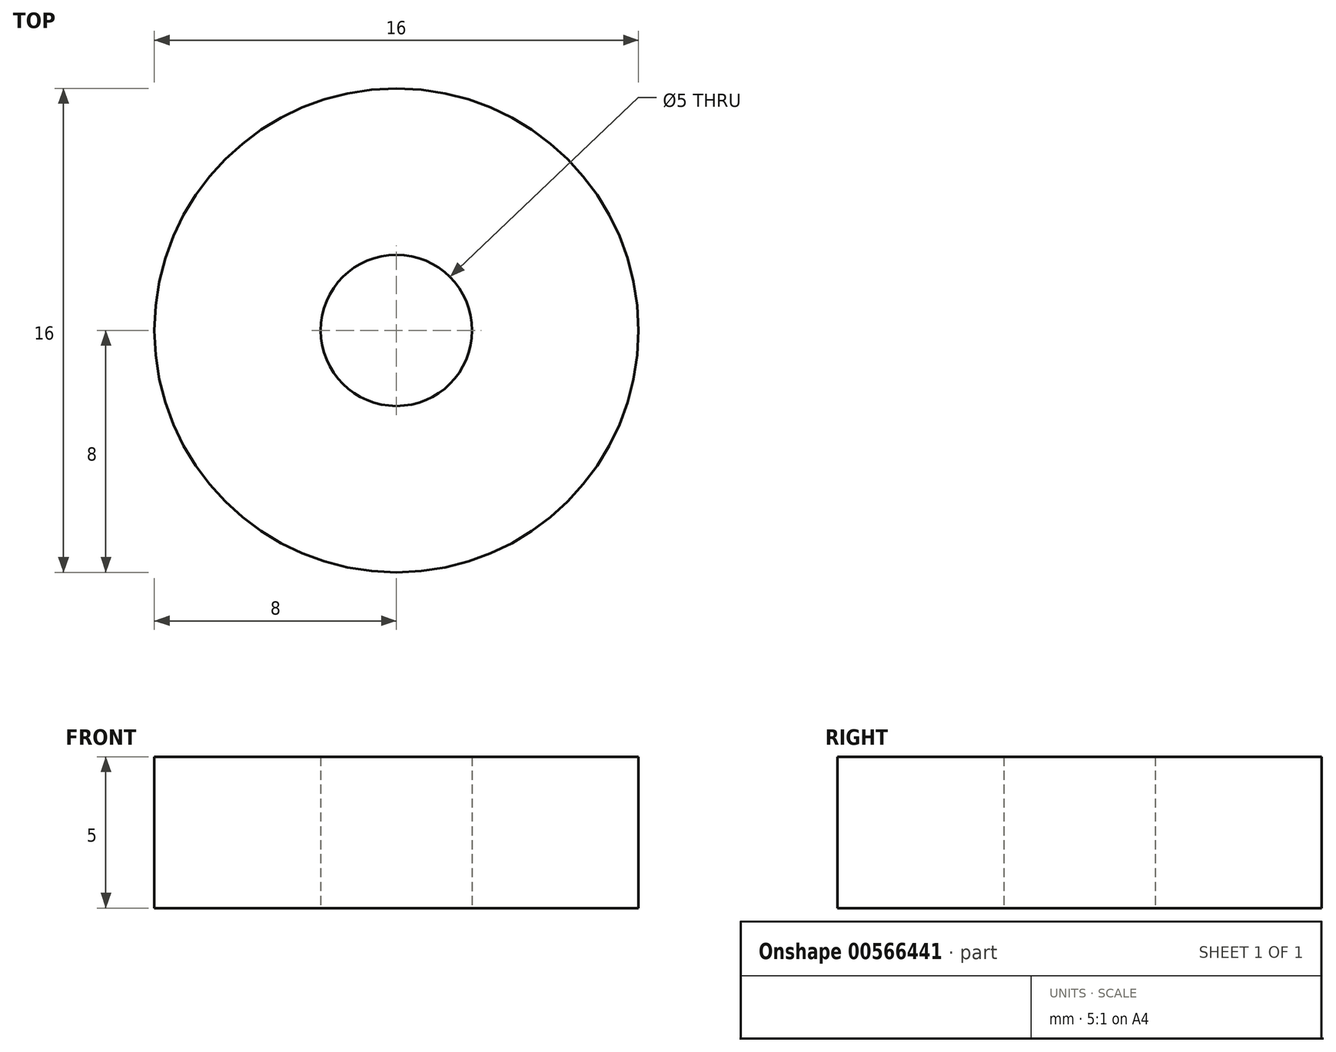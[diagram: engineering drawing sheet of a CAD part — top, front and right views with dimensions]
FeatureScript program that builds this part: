
annotation { "Feature Type Name" : "Feature", "Feature Type Description" : "" }
export const myFeature = defineFeature(function(context is Context, id is Id, definition is map)
    precondition{}
    {
        {
            var Q0;
            Q0=qCreatedBy(makeId("Top.planeOp"),FACE);
            var sketch = newSketch(context, id + "F0", { "sketchPlane" : qUnion([Q0])});
            skCircle(sketch, "E0", {"center": v(0, 0) * mm, "radius": 2.5 * mm});
            skCircle(sketch, "E1", {"center": v(0, 0) * mm, "radius": 8 * mm});
            skSolve(sketch);
        }
        {
            var Q0;
            Q0=qSketchRegion(id+"F0",true);
            extrude(context, id + "F1", {"entities" : qUnion([Q0]), "depth" : 5 * mm});
        }
    });
